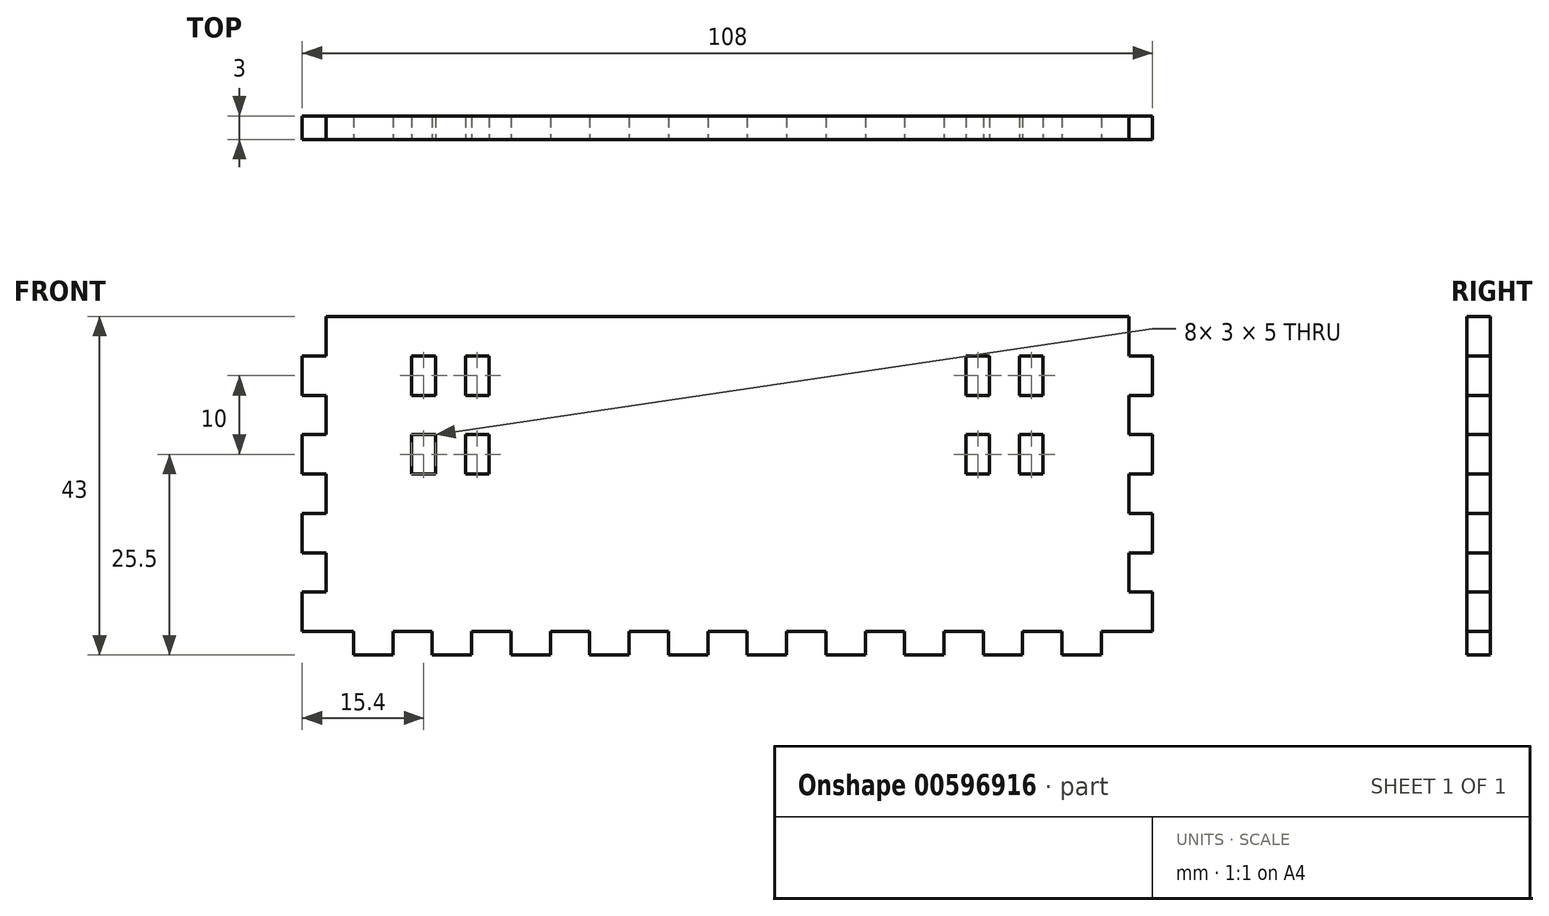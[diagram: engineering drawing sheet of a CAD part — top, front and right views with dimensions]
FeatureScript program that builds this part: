
annotation { "Feature Type Name" : "Feature", "Feature Type Description" : "" }
export const myFeature = defineFeature(function(context is Context, id is Id, definition is map)
    precondition{}
    {
        {
            var Q0;
            Q0=qCreatedBy(makeId("Front.planeOp"),FACE);
            var sketch = newSketch(context, id + "F0", { "sketchPlane" : qUnion([Q0])});
            skLineSegment(sketch, "E0.bottom", {"start": v(51, 20) * mm, "end": v(-51, 20) * mm});
            skLineSegment(sketch, "E0.top", {"start": v(51, -20) * mm, "end": v(-51, -20) * mm});
            skLineSegment(sketch, "E0.left", {"start": v(51, 20) * mm, "end": v(51, -20) * mm});
            skLineSegment(sketch, "E0.right", {"start": v(-51, 20) * mm, "end": v(-51, -20) * mm});
            skPoint(sketch, "E0.middle", {"position": v(0, 0) * mm});
            skSolve(sketch);
        }
        {
            var Q0;
            Q0=qSketchRegion(id+"F0",true);
            extrude(context, id + "F1", {"entities" : qUnion([Q0]), "depth" : 3 * mm, "offsetDistance" : 25 * mm});
        }
        {
            var Q0;
            Q0=makeQuery(id+"F1.opExtrude","CAP_FACE",FACE,{"disambiguationData":[OSD([sQuery(id+"F0.wireOp",EDGE,"E0.bottom"),sQuery(id+"F0.wireOp",EDGE,"E0.top"),sQuery(id+"F0.wireOp",EDGE,"E0.left"),sQuery(id+"F0.wireOp",EDGE,"E0.right")])],"isStart":false});
            var sketch = newSketch(context, id + "F2", { "sketchPlane" : qUnion([Q0])});
            skLineSegment(sketch, "E1.bottom", {"start": v(-51, -20) * mm, "end": v(-54, -20) * mm});
            skLineSegment(sketch, "E1.top", {"start": v(-51, -15) * mm, "end": v(-54, -15) * mm});
            skLineSegment(sketch, "E1.left", {"start": v(-51, -20) * mm, "end": v(-51, -15) * mm});
            skLineSegment(sketch, "E1.right", {"start": v(-54, -20) * mm, "end": v(-54, -15) * mm});
            skLineSegment(sketch, "E2.0.1.0", {"start": v(-51, -5) * mm, "end": v(-54, -5) * mm});
            skLineSegment(sketch, "E2.0.1.1", {"start": v(-54, -10) * mm, "end": v(-54, -5) * mm});
            skLineSegment(sketch, "E2.0.1.2", {"start": v(-51, -10) * mm, "end": v(-51, -5) * mm});
            skLineSegment(sketch, "E2.0.1.3", {"start": v(-51, -10) * mm, "end": v(-54, -10) * mm});
            skLineSegment(sketch, "E2.0.2.0", {"start": v(-51, 5) * mm, "end": v(-54, 5) * mm});
            skLineSegment(sketch, "E2.0.2.1", {"start": v(-54, 0) * mm, "end": v(-54, 5) * mm});
            skLineSegment(sketch, "E2.0.2.2", {"start": v(-51, 0) * mm, "end": v(-51, 5) * mm});
            skLineSegment(sketch, "E2.0.2.3", {"start": v(-51, 0) * mm, "end": v(-54, 0) * mm});
            skLineSegment(sketch, "E2.0.3.0", {"start": v(-51, 15) * mm, "end": v(-54, 15) * mm});
            skLineSegment(sketch, "E2.0.3.1", {"start": v(-54, 10) * mm, "end": v(-54, 15) * mm});
            skLineSegment(sketch, "E2.0.3.2", {"start": v(-51, 10) * mm, "end": v(-51, 15) * mm});
            skLineSegment(sketch, "E2.0.3.3", {"start": v(-51, 10) * mm, "end": v(-54, 10) * mm});
            skLineSegment(sketch, "E2.direction1", {"start": v(-54, -15) * mm, "end": v(-29, -15) * mm, "construction": true});
            skLineSegment(sketch, "E2.direction2", {"start": v(-54, -15) * mm, "end": v(-54, -5) * mm, "construction": true});
            skLineSegment(sketch, "E3.MirrorCS", {"start": v(54, -10) * mm, "end": v(54, -5) * mm});
            skLineSegment(sketch, "E4.MirrorCS", {"start": v(51, -5) * mm, "end": v(54, -5) * mm});
            skLineSegment(sketch, "E5.MirrorCS", {"start": v(51, -20) * mm, "end": v(51, -15) * mm});
            skLineSegment(sketch, "E6.MirrorCS", {"start": v(54, 10) * mm, "end": v(54, 15) * mm});
            skLineSegment(sketch, "E7.MirrorCS", {"start": v(51, -20) * mm, "end": v(54, -20) * mm});
            skLineSegment(sketch, "E8.MirrorCS", {"start": v(51, -15) * mm, "end": v(54, -15) * mm});
            skLineSegment(sketch, "E9.MirrorCS", {"start": v(54, -20) * mm, "end": v(54, -15) * mm});
            skLineSegment(sketch, "E10.MirrorCS", {"start": v(51, 15) * mm, "end": v(54, 15) * mm});
            skLineSegment(sketch, "E11.MirrorCS", {"start": v(51, 10) * mm, "end": v(54, 10) * mm});
            skLineSegment(sketch, "E12.MirrorCS", {"start": v(54, -15) * mm, "end": v(54, -5) * mm, "construction": true});
            skLineSegment(sketch, "E13.MirrorCS", {"start": v(51, 10) * mm, "end": v(51, 15) * mm});
            skLineSegment(sketch, "E14.MirrorCS", {"start": v(54, 0) * mm, "end": v(54, 5) * mm});
            skLineSegment(sketch, "E15.MirrorCS", {"start": v(51, 0) * mm, "end": v(51, 5) * mm});
            skLineSegment(sketch, "E16.MirrorCS", {"start": v(51, 0) * mm, "end": v(54, 0) * mm});
            skLineSegment(sketch, "E17.MirrorCS", {"start": v(51, -10) * mm, "end": v(51, -5) * mm});
            skLineSegment(sketch, "E18.MirrorCS", {"start": v(51, -10) * mm, "end": v(54, -10) * mm});
            skLineSegment(sketch, "E19.MirrorCS", {"start": v(51, 5) * mm, "end": v(54, 5) * mm});
            skSolve(sketch);
        }
        {
            var Q0;
            Q0=qSketchRegion(id+"F2",true);
            extrude(context, id + "F3", {"entities" : qUnion([Q0]), "operationType" : NewBodyOperationType.ADD, "oppositeDirection" : true, "depth" : 3 * mm, "offsetDistance" : 25 * mm});
        }
        {
            var Q0;
            Q0=makeQuery(id+"F3.boolean.opBoolean","MERGE",FACE,{"derivedFrom":[makeQuery(id+"F1.opExtrude","CAP_FACE",FACE,{"disambiguationData":[OSD([sQuery(id+"F0.wireOp",EDGE,"E0.bottom"),sQuery(id+"F0.wireOp",EDGE,"E0.top"),sQuery(id+"F0.wireOp",EDGE,"E0.left"),sQuery(id+"F0.wireOp",EDGE,"E0.right")])],"isStart":false}),makeQuery(id+"F3.opExtrude","CAP_FACE",FACE,{"disambiguationData":[OSD([sQuery(id+"F2.wireOp",EDGE,"E1.bottom"),sQuery(id+"F2.wireOp",EDGE,"E1.top"),sQuery(id+"F2.wireOp",EDGE,"E1.left"),sQuery(id+"F2.wireOp",EDGE,"E1.right")])],"isStart":true}),makeQuery(id+"F3.opExtrude","CAP_FACE",FACE,{"disambiguationData":[OSD([sQuery(id+"F2.wireOp",EDGE,"E2.0.1.0"),sQuery(id+"F2.wireOp",EDGE,"E2.0.1.1"),sQuery(id+"F2.wireOp",EDGE,"E2.0.1.2"),sQuery(id+"F2.wireOp",EDGE,"E2.0.1.3")])],"isStart":true}),makeQuery(id+"F3.opExtrude","CAP_FACE",FACE,{"disambiguationData":[OSD([sQuery(id+"F2.wireOp",EDGE,"E2.0.2.0"),sQuery(id+"F2.wireOp",EDGE,"E2.0.2.1"),sQuery(id+"F2.wireOp",EDGE,"E2.0.2.2"),sQuery(id+"F2.wireOp",EDGE,"E2.0.2.3")])],"isStart":true}),makeQuery(id+"F3.opExtrude","CAP_FACE",FACE,{"disambiguationData":[OSD([sQuery(id+"F2.wireOp",EDGE,"E2.0.3.0"),sQuery(id+"F2.wireOp",EDGE,"E2.0.3.1"),sQuery(id+"F2.wireOp",EDGE,"E2.0.3.2"),sQuery(id+"F2.wireOp",EDGE,"E2.0.3.3")])],"isStart":true}),makeQuery(id+"F3.opExtrude","CAP_FACE",FACE,{"disambiguationData":[OSD([sQuery(id+"F2.wireOp",EDGE,"E3.MirrorCS"),sQuery(id+"F2.wireOp",EDGE,"E4.MirrorCS"),sQuery(id+"F2.wireOp",EDGE,"E17.MirrorCS"),sQuery(id+"F2.wireOp",EDGE,"E18.MirrorCS")])],"isStart":true}),makeQuery(id+"F3.opExtrude","CAP_FACE",FACE,{"disambiguationData":[OSD([sQuery(id+"F2.wireOp",EDGE,"E5.MirrorCS"),sQuery(id+"F2.wireOp",EDGE,"E7.MirrorCS"),sQuery(id+"F2.wireOp",EDGE,"E8.MirrorCS"),sQuery(id+"F2.wireOp",EDGE,"E9.MirrorCS")])],"isStart":true}),makeQuery(id+"F3.opExtrude","CAP_FACE",FACE,{"disambiguationData":[OSD([sQuery(id+"F2.wireOp",EDGE,"E6.MirrorCS"),sQuery(id+"F2.wireOp",EDGE,"E10.MirrorCS"),sQuery(id+"F2.wireOp",EDGE,"E11.MirrorCS"),sQuery(id+"F2.wireOp",EDGE,"E13.MirrorCS")])],"isStart":true}),makeQuery(id+"F3.opExtrude","CAP_FACE",FACE,{"disambiguationData":[OSD([sQuery(id+"F2.wireOp",EDGE,"E14.MirrorCS"),sQuery(id+"F2.wireOp",EDGE,"E15.MirrorCS"),sQuery(id+"F2.wireOp",EDGE,"E16.MirrorCS"),sQuery(id+"F2.wireOp",EDGE,"E19.MirrorCS")])],"isStart":true})]});
            var sketch = newSketch(context, id + "F4", { "sketchPlane" : qUnion([Q0])});
            skLineSegment(sketch, "E20", {"start": v(0, -20) * mm, "end": v(0, -23) * mm, "construction": true});
            skPoint(sketch, "E20.endSnap0", {"position": v(0, -20) * mm});
            skLineSegment(sketch, "E21", {"start": v(0, -23) * mm, "end": v(2.5, -23) * mm, "construction": true});
            skLineSegment(sketch, "E22.bottom", {"start": v(2.5, -23) * mm, "end": v(7.5, -23) * mm});
            skLineSegment(sketch, "E22.top", {"start": v(2.5, -20) * mm, "end": v(7.5, -20) * mm});
            skLineSegment(sketch, "E22.left", {"start": v(2.5, -23) * mm, "end": v(2.5, -20) * mm});
            skLineSegment(sketch, "E22.right", {"start": v(7.5, -23) * mm, "end": v(7.5, -20) * mm});
            skLineSegment(sketch, "E23.1.0.0", {"start": v(12.5, -23) * mm, "end": v(17.5, -23) * mm});
            skLineSegment(sketch, "E23.1.0.1", {"start": v(12.5, -23) * mm, "end": v(12.5, -20) * mm});
            skLineSegment(sketch, "E23.1.0.2", {"start": v(17.5, -23) * mm, "end": v(17.5, -20) * mm});
            skLineSegment(sketch, "E23.1.0.3", {"start": v(12.5, -20) * mm, "end": v(17.5, -20) * mm});
            skLineSegment(sketch, "E23.2.0.0", {"start": v(22.5, -23) * mm, "end": v(27.5, -23) * mm});
            skLineSegment(sketch, "E23.2.0.1", {"start": v(22.5, -23) * mm, "end": v(22.5, -20) * mm});
            skLineSegment(sketch, "E23.2.0.2", {"start": v(27.5, -23) * mm, "end": v(27.5, -20) * mm});
            skLineSegment(sketch, "E23.2.0.3", {"start": v(22.5, -20) * mm, "end": v(27.5, -20) * mm});
            skLineSegment(sketch, "E23.3.0.0", {"start": v(32.5, -23) * mm, "end": v(37.5, -23) * mm});
            skLineSegment(sketch, "E23.3.0.1", {"start": v(32.5, -23) * mm, "end": v(32.5, -20) * mm});
            skLineSegment(sketch, "E23.3.0.2", {"start": v(37.5, -23) * mm, "end": v(37.5, -20) * mm});
            skLineSegment(sketch, "E23.3.0.3", {"start": v(32.5, -20) * mm, "end": v(37.5, -20) * mm});
            skLineSegment(sketch, "E23.4.0.0", {"start": v(42.5, -23) * mm, "end": v(47.5, -23) * mm});
            skLineSegment(sketch, "E23.4.0.1", {"start": v(42.5, -23) * mm, "end": v(42.5, -20) * mm});
            skLineSegment(sketch, "E23.4.0.2", {"start": v(47.5, -23) * mm, "end": v(47.5, -20) * mm});
            skLineSegment(sketch, "E23.4.0.3", {"start": v(42.5, -20) * mm, "end": v(47.5, -20) * mm});
            skLineSegment(sketch, "E23.direction1", {"start": v(2.5, -23) * mm, "end": v(12.5, -23) * mm, "construction": true});
            skLineSegment(sketch, "E24.MirrorCS", {"start": v(-27.5, -23) * mm, "end": v(-27.5, -20) * mm});
            skLineSegment(sketch, "E25.MirrorCS", {"start": v(-22.5, -23) * mm, "end": v(-22.5, -20) * mm});
            skLineSegment(sketch, "E26.MirrorCS", {"start": v(-17.5, -23) * mm, "end": v(-17.5, -20) * mm});
            skLineSegment(sketch, "E27.MirrorCS", {"start": v(-12.5, -23) * mm, "end": v(-12.5, -20) * mm});
            skLineSegment(sketch, "E28.MirrorCS", {"start": v(-7.5, -23) * mm, "end": v(-7.5, -20) * mm});
            skLineSegment(sketch, "E29.MirrorCS", {"start": v(-2.5, -23) * mm, "end": v(-2.5, -20) * mm});
            skLineSegment(sketch, "E30.MirrorCS", {"start": v(-32.5, -23) * mm, "end": v(-32.5, -20) * mm});
            skLineSegment(sketch, "E31.MirrorCS", {"start": v(-47.5, -23) * mm, "end": v(-47.5, -20) * mm});
            skLineSegment(sketch, "E32.MirrorCS", {"start": v(-37.5, -23) * mm, "end": v(-37.5, -20) * mm});
            skLineSegment(sketch, "E33.MirrorCS", {"start": v(-42.5, -23) * mm, "end": v(-42.5, -20) * mm});
            skLineSegment(sketch, "E34.MirrorCS", {"start": v(-2.5, -23) * mm, "end": v(-7.5, -23) * mm});
            skLineSegment(sketch, "E35.MirrorCS", {"start": v(-32.5, -20) * mm, "end": v(-37.5, -20) * mm});
            skLineSegment(sketch, "E36.MirrorCS", {"start": v(-42.5, -20) * mm, "end": v(-47.5, -20) * mm});
            skLineSegment(sketch, "E37.MirrorCS", {"start": v(-22.5, -23) * mm, "end": v(-27.5, -23) * mm});
            skLineSegment(sketch, "E38.MirrorCS", {"start": v(-12.5, -20) * mm, "end": v(-17.5, -20) * mm});
            skLineSegment(sketch, "E39.MirrorCS", {"start": v(-12.5, -23) * mm, "end": v(-17.5, -23) * mm});
            skLineSegment(sketch, "E40.MirrorCS", {"start": v(-2.5, -20) * mm, "end": v(-7.5, -20) * mm});
            skLineSegment(sketch, "E41.MirrorCS", {"start": v(-32.5, -23) * mm, "end": v(-37.5, -23) * mm});
            skLineSegment(sketch, "E42.MirrorCS", {"start": v(-22.5, -20) * mm, "end": v(-27.5, -20) * mm});
            skLineSegment(sketch, "E43.MirrorCS", {"start": v(-42.5, -23) * mm, "end": v(-47.5, -23) * mm});
            skLineSegment(sketch, "E44.MirrorCS", {"start": v(-2.5, -23) * mm, "end": v(-12.5, -23) * mm, "construction": true});
            skSolve(sketch);
        }
        {
            var Q0;
            Q0=qSketchRegion(id+"F4",true);
            extrude(context, id + "F5", {"entities" : qUnion([Q0]), "operationType" : NewBodyOperationType.ADD, "oppositeDirection" : true, "depth" : 3 * mm, "offsetDistance" : 25 * mm});
        }
        {
            var Q0;
            Q0=makeQuery(id+"F5.boolean.opBoolean","MERGE",FACE,{"derivedFrom":[makeQuery(id+"F3.boolean.opBoolean","MERGE",FACE,{"derivedFrom":[makeQuery(id+"F1.opExtrude","CAP_FACE",FACE,{"disambiguationData":[OSD([sQuery(id+"F0.wireOp",EDGE,"E0.bottom"),sQuery(id+"F0.wireOp",EDGE,"E0.top"),sQuery(id+"F0.wireOp",EDGE,"E0.left"),sQuery(id+"F0.wireOp",EDGE,"E0.right")])],"isStart":false}),makeQuery(id+"F3.opExtrude","CAP_FACE",FACE,{"disambiguationData":[OSD([sQuery(id+"F2.wireOp",EDGE,"E1.bottom"),sQuery(id+"F2.wireOp",EDGE,"E1.top"),sQuery(id+"F2.wireOp",EDGE,"E1.left"),sQuery(id+"F2.wireOp",EDGE,"E1.right")])],"isStart":true}),makeQuery(id+"F3.opExtrude","CAP_FACE",FACE,{"disambiguationData":[OSD([sQuery(id+"F2.wireOp",EDGE,"E2.0.1.0"),sQuery(id+"F2.wireOp",EDGE,"E2.0.1.1"),sQuery(id+"F2.wireOp",EDGE,"E2.0.1.2"),sQuery(id+"F2.wireOp",EDGE,"E2.0.1.3")])],"isStart":true}),makeQuery(id+"F3.opExtrude","CAP_FACE",FACE,{"disambiguationData":[OSD([sQuery(id+"F2.wireOp",EDGE,"E2.0.2.0"),sQuery(id+"F2.wireOp",EDGE,"E2.0.2.1"),sQuery(id+"F2.wireOp",EDGE,"E2.0.2.2"),sQuery(id+"F2.wireOp",EDGE,"E2.0.2.3")])],"isStart":true}),makeQuery(id+"F3.opExtrude","CAP_FACE",FACE,{"disambiguationData":[OSD([sQuery(id+"F2.wireOp",EDGE,"E2.0.3.0"),sQuery(id+"F2.wireOp",EDGE,"E2.0.3.1"),sQuery(id+"F2.wireOp",EDGE,"E2.0.3.2"),sQuery(id+"F2.wireOp",EDGE,"E2.0.3.3")])],"isStart":true}),makeQuery(id+"F3.opExtrude","CAP_FACE",FACE,{"disambiguationData":[OSD([sQuery(id+"F2.wireOp",EDGE,"E3.MirrorCS"),sQuery(id+"F2.wireOp",EDGE,"E4.MirrorCS"),sQuery(id+"F2.wireOp",EDGE,"E17.MirrorCS"),sQuery(id+"F2.wireOp",EDGE,"E18.MirrorCS")])],"isStart":true}),makeQuery(id+"F3.opExtrude","CAP_FACE",FACE,{"disambiguationData":[OSD([sQuery(id+"F2.wireOp",EDGE,"E5.MirrorCS"),sQuery(id+"F2.wireOp",EDGE,"E7.MirrorCS"),sQuery(id+"F2.wireOp",EDGE,"E8.MirrorCS"),sQuery(id+"F2.wireOp",EDGE,"E9.MirrorCS")])],"isStart":true}),makeQuery(id+"F3.opExtrude","CAP_FACE",FACE,{"disambiguationData":[OSD([sQuery(id+"F2.wireOp",EDGE,"E6.MirrorCS"),sQuery(id+"F2.wireOp",EDGE,"E10.MirrorCS"),sQuery(id+"F2.wireOp",EDGE,"E11.MirrorCS"),sQuery(id+"F2.wireOp",EDGE,"E13.MirrorCS")])],"isStart":true}),makeQuery(id+"F3.opExtrude","CAP_FACE",FACE,{"disambiguationData":[OSD([sQuery(id+"F2.wireOp",EDGE,"E14.MirrorCS"),sQuery(id+"F2.wireOp",EDGE,"E15.MirrorCS"),sQuery(id+"F2.wireOp",EDGE,"E16.MirrorCS"),sQuery(id+"F2.wireOp",EDGE,"E19.MirrorCS")])],"isStart":true})]}),makeQuery(id+"F5.opExtrude","CAP_FACE",FACE,{"disambiguationData":[OSD([sQuery(id+"F4.wireOp",EDGE,"E22.bottom"),sQuery(id+"F4.wireOp",EDGE,"E22.top"),sQuery(id+"F4.wireOp",EDGE,"E22.left"),sQuery(id+"F4.wireOp",EDGE,"E22.right")])],"isStart":true}),makeQuery(id+"F5.opExtrude","CAP_FACE",FACE,{"disambiguationData":[OSD([sQuery(id+"F4.wireOp",EDGE,"E23.1.0.0"),sQuery(id+"F4.wireOp",EDGE,"E23.1.0.1"),sQuery(id+"F4.wireOp",EDGE,"E23.1.0.2"),sQuery(id+"F4.wireOp",EDGE,"E23.1.0.3")])],"isStart":true}),makeQuery(id+"F5.opExtrude","CAP_FACE",FACE,{"disambiguationData":[OSD([sQuery(id+"F4.wireOp",EDGE,"E23.2.0.0"),sQuery(id+"F4.wireOp",EDGE,"E23.2.0.1"),sQuery(id+"F4.wireOp",EDGE,"E23.2.0.2"),sQuery(id+"F4.wireOp",EDGE,"E23.2.0.3")])],"isStart":true}),makeQuery(id+"F5.opExtrude","CAP_FACE",FACE,{"disambiguationData":[OSD([sQuery(id+"F4.wireOp",EDGE,"E23.3.0.0"),sQuery(id+"F4.wireOp",EDGE,"E23.3.0.1"),sQuery(id+"F4.wireOp",EDGE,"E23.3.0.2"),sQuery(id+"F4.wireOp",EDGE,"E23.3.0.3")])],"isStart":true}),makeQuery(id+"F5.opExtrude","CAP_FACE",FACE,{"disambiguationData":[OSD([sQuery(id+"F4.wireOp",EDGE,"E23.4.0.0"),sQuery(id+"F4.wireOp",EDGE,"E23.4.0.1"),sQuery(id+"F4.wireOp",EDGE,"E23.4.0.2"),sQuery(id+"F4.wireOp",EDGE,"E23.4.0.3")])],"isStart":true}),makeQuery(id+"F5.opExtrude","CAP_FACE",FACE,{"disambiguationData":[OSD([sQuery(id+"F4.wireOp",EDGE,"E24.MirrorCS"),sQuery(id+"F4.wireOp",EDGE,"E25.MirrorCS"),sQuery(id+"F4.wireOp",EDGE,"E37.MirrorCS"),sQuery(id+"F4.wireOp",EDGE,"E42.MirrorCS")])],"isStart":true}),makeQuery(id+"F5.opExtrude","CAP_FACE",FACE,{"disambiguationData":[OSD([sQuery(id+"F4.wireOp",EDGE,"E26.MirrorCS"),sQuery(id+"F4.wireOp",EDGE,"E27.MirrorCS"),sQuery(id+"F4.wireOp",EDGE,"E38.MirrorCS"),sQuery(id+"F4.wireOp",EDGE,"E39.MirrorCS")])],"isStart":true}),makeQuery(id+"F5.opExtrude","CAP_FACE",FACE,{"disambiguationData":[OSD([sQuery(id+"F4.wireOp",EDGE,"E28.MirrorCS"),sQuery(id+"F4.wireOp",EDGE,"E29.MirrorCS"),sQuery(id+"F4.wireOp",EDGE,"E34.MirrorCS"),sQuery(id+"F4.wireOp",EDGE,"E40.MirrorCS")])],"isStart":true}),makeQuery(id+"F5.opExtrude","CAP_FACE",FACE,{"disambiguationData":[OSD([sQuery(id+"F4.wireOp",EDGE,"E30.MirrorCS"),sQuery(id+"F4.wireOp",EDGE,"E32.MirrorCS"),sQuery(id+"F4.wireOp",EDGE,"E35.MirrorCS"),sQuery(id+"F4.wireOp",EDGE,"E41.MirrorCS")])],"isStart":true}),makeQuery(id+"F5.opExtrude","CAP_FACE",FACE,{"disambiguationData":[OSD([sQuery(id+"F4.wireOp",EDGE,"E31.MirrorCS"),sQuery(id+"F4.wireOp",EDGE,"E33.MirrorCS"),sQuery(id+"F4.wireOp",EDGE,"E36.MirrorCS"),sQuery(id+"F4.wireOp",EDGE,"E43.MirrorCS")])],"isStart":true})]});
            var sketch = newSketch(context, id + "F6", { "sketchPlane" : qUnion([Q0])});
            skLineSegment(sketch, "E45", {"start": v(0, 20) * mm, "end": v(-32, 20) * mm, "construction": true});
            skLineSegment(sketch, "E46", {"start": v(-32, 20) * mm, "end": v(-32, 12.5) * mm, "construction": true});
            skLineSegment(sketch, "E47.bottom", {"start": v(-33.5, 10) * mm, "end": v(-30.5, 10) * mm});
            skLineSegment(sketch, "E47.top", {"start": v(-33.5, 15) * mm, "end": v(-30.5, 15) * mm});
            skLineSegment(sketch, "E47.left", {"start": v(-33.5, 10) * mm, "end": v(-33.5, 15) * mm});
            skLineSegment(sketch, "E47.right", {"start": v(-30.5, 10) * mm, "end": v(-30.5, 15) * mm});
            skPoint(sketch, "E47.middle", {"position": v(-32, 12.5) * mm});
            skLineSegment(sketch, "E48.0.1.0", {"start": v(-33.5, 0) * mm, "end": v(-30.5, 0) * mm});
            skLineSegment(sketch, "E48.0.1.1", {"start": v(-33.5, 0) * mm, "end": v(-33.5, 5) * mm});
            skLineSegment(sketch, "E48.0.1.2", {"start": v(-30.5, 0) * mm, "end": v(-30.5, 5) * mm});
            skLineSegment(sketch, "E48.0.1.3", {"start": v(-33.5, 5) * mm, "end": v(-30.5, 5) * mm});
            skLineSegment(sketch, "E48.direction1", {"start": v(-33.5, 10) * mm, "end": v(-8.5, 10) * mm, "construction": true});
            skLineSegment(sketch, "E48.direction2", {"start": v(-33.5, 10) * mm, "end": v(-33.5, 0) * mm, "construction": true});
            skLineSegment(sketch, "E49.MirrorCS", {"start": v(33.5, 0) * mm, "end": v(30.5, 0) * mm});
            skLineSegment(sketch, "E50.MirrorCS", {"start": v(33.5, 15) * mm, "end": v(30.5, 15) * mm});
            skLineSegment(sketch, "E51.MirrorCS", {"start": v(33.5, 10) * mm, "end": v(30.5, 10) * mm});
            skLineSegment(sketch, "E52.MirrorCS", {"start": v(33.5, 5) * mm, "end": v(30.5, 5) * mm});
            skLineSegment(sketch, "E53.MirrorCS", {"start": v(33.5, 0) * mm, "end": v(33.5, 5) * mm});
            skLineSegment(sketch, "E54.MirrorCS", {"start": v(30.5, 10) * mm, "end": v(30.5, 15) * mm});
            skLineSegment(sketch, "E55.MirrorCS", {"start": v(33.5, 10) * mm, "end": v(33.5, 15) * mm});
            skLineSegment(sketch, "E56.MirrorCS", {"start": v(32, 20) * mm, "end": v(32, 12.5) * mm, "construction": true});
            skLineSegment(sketch, "E57.MirrorCS", {"start": v(30.5, 0) * mm, "end": v(30.5, 5) * mm});
            skLineSegment(sketch, "E58.MirrorCS", {"start": v(33.5, 10) * mm, "end": v(33.5, 0) * mm, "construction": true});
            skPoint(sketch, "E59.MirrorP", {"position": v(32, 12.5) * mm});
            skLineSegment(sketch, "E60", {"start": v(-32, 20) * mm, "end": v(-35.2, 20) * mm, "construction": true});
            skLineSegment(sketch, "E61", {"start": v(-35.2, 20) * mm, "end": v(-35.2, 16.67) * mm, "construction": true});
            skLineSegment(sketch, "E62.MirrorCS", {"start": v(-36.9, 0) * mm, "end": v(-36.9, 5) * mm});
            skLineSegment(sketch, "E63.MirrorCS", {"start": v(-36.9, 0) * mm, "end": v(-39.9, 0) * mm});
            skLineSegment(sketch, "E64.MirrorCS", {"start": v(-39.9, 0) * mm, "end": v(-39.9, 5) * mm});
            skLineSegment(sketch, "E65.MirrorCS", {"start": v(-36.9, 5) * mm, "end": v(-39.9, 5) * mm});
            skLineSegment(sketch, "E66.MirrorCS", {"start": v(-36.9, 10) * mm, "end": v(-36.9, 0) * mm, "construction": true});
            skPoint(sketch, "E67.MirrorP", {"position": v(-38.4, 12.5) * mm});
            skLineSegment(sketch, "E68.MirrorCS", {"start": v(-39.9, 10) * mm, "end": v(-39.9, 15) * mm});
            skLineSegment(sketch, "E69.MirrorCS", {"start": v(-36.9, 10) * mm, "end": v(-36.9, 15) * mm});
            skLineSegment(sketch, "E70.MirrorCS", {"start": v(-36.9, 15) * mm, "end": v(-39.9, 15) * mm});
            skLineSegment(sketch, "E71.MirrorCS", {"start": v(-36.9, 10) * mm, "end": v(-39.9, 10) * mm});
            skLineSegment(sketch, "E72.MirrorCS", {"start": v(36.9, 10) * mm, "end": v(39.9, 10) * mm});
            skPoint(sketch, "E73.MirrorP", {"position": v(38.4, 12.5) * mm});
            skLineSegment(sketch, "E74.MirrorCS", {"start": v(39.9, 0) * mm, "end": v(39.9, 5) * mm});
            skLineSegment(sketch, "E75.MirrorCS", {"start": v(36.9, 15) * mm, "end": v(39.9, 15) * mm});
            skLineSegment(sketch, "E76.MirrorCS", {"start": v(36.9, 0) * mm, "end": v(39.9, 0) * mm});
            skLineSegment(sketch, "E77.MirrorCS", {"start": v(36.9, 0) * mm, "end": v(36.9, 5) * mm});
            skLineSegment(sketch, "E78.MirrorCS", {"start": v(36.9, 10) * mm, "end": v(36.9, 15) * mm});
            skLineSegment(sketch, "E79.MirrorCS", {"start": v(36.9, 5) * mm, "end": v(39.9, 5) * mm});
            skLineSegment(sketch, "E80.MirrorCS", {"start": v(36.9, 10) * mm, "end": v(36.9, 0) * mm, "construction": true});
            skLineSegment(sketch, "E81.MirrorCS", {"start": v(39.9, 10) * mm, "end": v(39.9, 15) * mm});
            skSolve(sketch);
        }
        {
            var Q0;
            Q0 = qSketchRegion(id + "F6", true);
            extrude(context, id + "F7", {"entities" : qUnion([Q0]), "operationType" : NewBodyOperationType.REMOVE, "oppositeDirection" : true, "depth" : 25 * mm, "offsetDistance" : 25 * mm});
        }
        {
            var Q0;
            Q0=makeQuery(id+"F5.boolean.opBoolean","MERGE",FACE,{"derivedFrom":[makeQuery(id+"F3.boolean.opBoolean","MERGE",FACE,{"derivedFrom":[makeQuery(id+"F1.opExtrude","CAP_FACE",FACE,{"disambiguationData":[OSD([sQuery(id+"F0.wireOp",EDGE,"E0.bottom"),sQuery(id+"F0.wireOp",EDGE,"E0.top"),sQuery(id+"F0.wireOp",EDGE,"E0.left"),sQuery(id+"F0.wireOp",EDGE,"E0.right")])],"isStart":false}),makeQuery(id+"F3.opExtrude","CAP_FACE",FACE,{"disambiguationData":[OSD([sQuery(id+"F2.wireOp",EDGE,"E1.bottom"),sQuery(id+"F2.wireOp",EDGE,"E1.top"),sQuery(id+"F2.wireOp",EDGE,"E1.left"),sQuery(id+"F2.wireOp",EDGE,"E1.right")])],"isStart":true}),makeQuery(id+"F3.opExtrude","CAP_FACE",FACE,{"disambiguationData":[OSD([sQuery(id+"F2.wireOp",EDGE,"E2.0.1.0"),sQuery(id+"F2.wireOp",EDGE,"E2.0.1.1"),sQuery(id+"F2.wireOp",EDGE,"E2.0.1.2"),sQuery(id+"F2.wireOp",EDGE,"E2.0.1.3")])],"isStart":true}),makeQuery(id+"F3.opExtrude","CAP_FACE",FACE,{"disambiguationData":[OSD([sQuery(id+"F2.wireOp",EDGE,"E2.0.2.0"),sQuery(id+"F2.wireOp",EDGE,"E2.0.2.1"),sQuery(id+"F2.wireOp",EDGE,"E2.0.2.2"),sQuery(id+"F2.wireOp",EDGE,"E2.0.2.3")])],"isStart":true}),makeQuery(id+"F3.opExtrude","CAP_FACE",FACE,{"disambiguationData":[OSD([sQuery(id+"F2.wireOp",EDGE,"E2.0.3.0"),sQuery(id+"F2.wireOp",EDGE,"E2.0.3.1"),sQuery(id+"F2.wireOp",EDGE,"E2.0.3.2"),sQuery(id+"F2.wireOp",EDGE,"E2.0.3.3")])],"isStart":true}),makeQuery(id+"F3.opExtrude","CAP_FACE",FACE,{"disambiguationData":[OSD([sQuery(id+"F2.wireOp",EDGE,"E3.MirrorCS"),sQuery(id+"F2.wireOp",EDGE,"E4.MirrorCS"),sQuery(id+"F2.wireOp",EDGE,"E17.MirrorCS"),sQuery(id+"F2.wireOp",EDGE,"E18.MirrorCS")])],"isStart":true}),makeQuery(id+"F3.opExtrude","CAP_FACE",FACE,{"disambiguationData":[OSD([sQuery(id+"F2.wireOp",EDGE,"E5.MirrorCS"),sQuery(id+"F2.wireOp",EDGE,"E7.MirrorCS"),sQuery(id+"F2.wireOp",EDGE,"E8.MirrorCS"),sQuery(id+"F2.wireOp",EDGE,"E9.MirrorCS")])],"isStart":true}),makeQuery(id+"F3.opExtrude","CAP_FACE",FACE,{"disambiguationData":[OSD([sQuery(id+"F2.wireOp",EDGE,"E6.MirrorCS"),sQuery(id+"F2.wireOp",EDGE,"E10.MirrorCS"),sQuery(id+"F2.wireOp",EDGE,"E11.MirrorCS"),sQuery(id+"F2.wireOp",EDGE,"E13.MirrorCS")])],"isStart":true}),makeQuery(id+"F3.opExtrude","CAP_FACE",FACE,{"disambiguationData":[OSD([sQuery(id+"F2.wireOp",EDGE,"E14.MirrorCS"),sQuery(id+"F2.wireOp",EDGE,"E15.MirrorCS"),sQuery(id+"F2.wireOp",EDGE,"E16.MirrorCS"),sQuery(id+"F2.wireOp",EDGE,"E19.MirrorCS")])],"isStart":true})]}),makeQuery(id+"F5.opExtrude","CAP_FACE",FACE,{"disambiguationData":[OSD([sQuery(id+"F4.wireOp",EDGE,"E22.bottom"),sQuery(id+"F4.wireOp",EDGE,"E22.top"),sQuery(id+"F4.wireOp",EDGE,"E22.left"),sQuery(id+"F4.wireOp",EDGE,"E22.right")])],"isStart":true}),makeQuery(id+"F5.opExtrude","CAP_FACE",FACE,{"disambiguationData":[OSD([sQuery(id+"F4.wireOp",EDGE,"E23.1.0.0"),sQuery(id+"F4.wireOp",EDGE,"E23.1.0.1"),sQuery(id+"F4.wireOp",EDGE,"E23.1.0.2"),sQuery(id+"F4.wireOp",EDGE,"E23.1.0.3")])],"isStart":true}),makeQuery(id+"F5.opExtrude","CAP_FACE",FACE,{"disambiguationData":[OSD([sQuery(id+"F4.wireOp",EDGE,"E23.2.0.0"),sQuery(id+"F4.wireOp",EDGE,"E23.2.0.1"),sQuery(id+"F4.wireOp",EDGE,"E23.2.0.2"),sQuery(id+"F4.wireOp",EDGE,"E23.2.0.3")])],"isStart":true}),makeQuery(id+"F5.opExtrude","CAP_FACE",FACE,{"disambiguationData":[OSD([sQuery(id+"F4.wireOp",EDGE,"E23.3.0.0"),sQuery(id+"F4.wireOp",EDGE,"E23.3.0.1"),sQuery(id+"F4.wireOp",EDGE,"E23.3.0.2"),sQuery(id+"F4.wireOp",EDGE,"E23.3.0.3")])],"isStart":true}),makeQuery(id+"F5.opExtrude","CAP_FACE",FACE,{"disambiguationData":[OSD([sQuery(id+"F4.wireOp",EDGE,"E23.4.0.0"),sQuery(id+"F4.wireOp",EDGE,"E23.4.0.1"),sQuery(id+"F4.wireOp",EDGE,"E23.4.0.2"),sQuery(id+"F4.wireOp",EDGE,"E23.4.0.3")])],"isStart":true}),makeQuery(id+"F5.opExtrude","CAP_FACE",FACE,{"disambiguationData":[OSD([sQuery(id+"F4.wireOp",EDGE,"E24.MirrorCS"),sQuery(id+"F4.wireOp",EDGE,"E25.MirrorCS"),sQuery(id+"F4.wireOp",EDGE,"E37.MirrorCS"),sQuery(id+"F4.wireOp",EDGE,"E42.MirrorCS")])],"isStart":true}),makeQuery(id+"F5.opExtrude","CAP_FACE",FACE,{"disambiguationData":[OSD([sQuery(id+"F4.wireOp",EDGE,"E26.MirrorCS"),sQuery(id+"F4.wireOp",EDGE,"E27.MirrorCS"),sQuery(id+"F4.wireOp",EDGE,"E38.MirrorCS"),sQuery(id+"F4.wireOp",EDGE,"E39.MirrorCS")])],"isStart":true}),makeQuery(id+"F5.opExtrude","CAP_FACE",FACE,{"disambiguationData":[OSD([sQuery(id+"F4.wireOp",EDGE,"E28.MirrorCS"),sQuery(id+"F4.wireOp",EDGE,"E29.MirrorCS"),sQuery(id+"F4.wireOp",EDGE,"E34.MirrorCS"),sQuery(id+"F4.wireOp",EDGE,"E40.MirrorCS")])],"isStart":true}),makeQuery(id+"F5.opExtrude","CAP_FACE",FACE,{"disambiguationData":[OSD([sQuery(id+"F4.wireOp",EDGE,"E30.MirrorCS"),sQuery(id+"F4.wireOp",EDGE,"E32.MirrorCS"),sQuery(id+"F4.wireOp",EDGE,"E35.MirrorCS"),sQuery(id+"F4.wireOp",EDGE,"E41.MirrorCS")])],"isStart":true}),makeQuery(id+"F5.opExtrude","CAP_FACE",FACE,{"disambiguationData":[OSD([sQuery(id+"F4.wireOp",EDGE,"E31.MirrorCS"),sQuery(id+"F4.wireOp",EDGE,"E33.MirrorCS"),sQuery(id+"F4.wireOp",EDGE,"E36.MirrorCS"),sQuery(id+"F4.wireOp",EDGE,"E43.MirrorCS")])],"isStart":true})]});
            var sketch = newSketch(context, id + "F8", { "sketchPlane" : qUnion([Q0])});
            skLineSegment(sketch, "E82.bottom", {"start": v(-33.5, 15) * mm, "end": v(-33.3, 15) * mm});
            skLineSegment(sketch, "E82.top", {"start": v(-33.5, 10) * mm, "end": v(-33.3, 10) * mm});
            skLineSegment(sketch, "E82.left", {"start": v(-33.5, 15) * mm, "end": v(-33.5, 10) * mm});
            skLineSegment(sketch, "E82.right", {"start": v(-33.3, 15) * mm, "end": v(-33.3, 10) * mm});
            skLineSegment(sketch, "E83.bottom", {"start": v(-36.9, 15) * mm, "end": v(-37.1, 15) * mm});
            skLineSegment(sketch, "E83.top", {"start": v(-36.9, 10) * mm, "end": v(-37.1, 10) * mm});
            skLineSegment(sketch, "E83.left", {"start": v(-36.9, 15) * mm, "end": v(-36.9, 10) * mm});
            skLineSegment(sketch, "E83.right", {"start": v(-37.1, 15) * mm, "end": v(-37.1, 10) * mm});
            skLineSegment(sketch, "E84", {"start": v(-36.9, 5) * mm, "end": v(-33.5, 5) * mm, "construction": true});
            skLineSegment(sketch, "E85", {"start": v(-33.5, 5) * mm, "end": v(-35.2, 5) * mm, "construction": true});
            skLineSegment(sketch, "E86", {"start": v(-35.2, 5) * mm, "end": v(-35.2, 10) * mm, "construction": true});
            skLineSegment(sketch, "E87", {"start": v(-35.2, 10) * mm, "end": v(-35.2, 7.5) * mm, "construction": true});
            skLineSegment(sketch, "E88", {"start": v(-35.2, 7.5) * mm, "end": v(-33.5, 7.5) * mm, "construction": true});
            skLineSegment(sketch, "E89.MirrorCS", {"start": v(-36.9, 5) * mm, "end": v(-37.1, 5) * mm});
            skLineSegment(sketch, "E90.MirrorCS", {"start": v(-36.9, 0) * mm, "end": v(-37.1, 0) * mm});
            skLineSegment(sketch, "E91.MirrorCS", {"start": v(-33.5, 5) * mm, "end": v(-33.3, 5) * mm});
            skLineSegment(sketch, "E92.MirrorCS", {"start": v(-33.5, 0) * mm, "end": v(-33.3, 0) * mm});
            skLineSegment(sketch, "E93.MirrorCS", {"start": v(-36.9, 0) * mm, "end": v(-36.9, 5) * mm});
            skLineSegment(sketch, "E94.MirrorCS", {"start": v(-33.5, 0) * mm, "end": v(-33.5, 5) * mm});
            skLineSegment(sketch, "E95.MirrorCS", {"start": v(-37.1, 0) * mm, "end": v(-37.1, 5) * mm});
            skLineSegment(sketch, "E96.MirrorCS", {"start": v(-33.3, 0) * mm, "end": v(-33.3, 5) * mm});
            skLineSegment(sketch, "E97.MirrorCS", {"start": v(33.5, 5) * mm, "end": v(33.3, 5) * mm});
            skLineSegment(sketch, "E98.MirrorCS", {"start": v(33.5, 0) * mm, "end": v(33.3, 0) * mm});
            skLineSegment(sketch, "E99.MirrorCS", {"start": v(36.9, 5) * mm, "end": v(37.1, 5) * mm});
            skLineSegment(sketch, "E100.MirrorCS", {"start": v(36.9, 0) * mm, "end": v(37.1, 0) * mm});
            skLineSegment(sketch, "E101.MirrorCS", {"start": v(33.5, 10) * mm, "end": v(33.3, 10) * mm});
            skLineSegment(sketch, "E102.MirrorCS", {"start": v(33.5, 15) * mm, "end": v(33.3, 15) * mm});
            skLineSegment(sketch, "E103.MirrorCS", {"start": v(33.5, 0) * mm, "end": v(33.5, 5) * mm});
            skLineSegment(sketch, "E104.MirrorCS", {"start": v(36.9, 5) * mm, "end": v(33.5, 5) * mm, "construction": true});
            skLineSegment(sketch, "E105.MirrorCS", {"start": v(33.5, 5) * mm, "end": v(35.2, 5) * mm, "construction": true});
            skLineSegment(sketch, "E106.MirrorCS", {"start": v(36.9, 10) * mm, "end": v(37.1, 10) * mm});
            skLineSegment(sketch, "E107.MirrorCS", {"start": v(36.9, 15) * mm, "end": v(37.1, 15) * mm});
            skLineSegment(sketch, "E108.MirrorCS", {"start": v(37.1, 0) * mm, "end": v(37.1, 5) * mm});
            skLineSegment(sketch, "E109.MirrorCS", {"start": v(35.2, 7.5) * mm, "end": v(33.5, 7.5) * mm, "construction": true});
            skLineSegment(sketch, "E110.MirrorCS", {"start": v(36.9, 0) * mm, "end": v(36.9, 5) * mm});
            skLineSegment(sketch, "E111.MirrorCS", {"start": v(33.3, 0) * mm, "end": v(33.3, 5) * mm});
            skLineSegment(sketch, "E112.MirrorCS", {"start": v(33.5, 15) * mm, "end": v(33.5, 10) * mm});
            skLineSegment(sketch, "E113.MirrorCS", {"start": v(35.2, 5) * mm, "end": v(35.2, 10) * mm, "construction": true});
            skLineSegment(sketch, "E114.MirrorCS", {"start": v(37.1, 15) * mm, "end": v(37.1, 10) * mm});
            skLineSegment(sketch, "E115.MirrorCS", {"start": v(35.2, 10) * mm, "end": v(35.2, 7.5) * mm, "construction": true});
            skLineSegment(sketch, "E116.MirrorCS", {"start": v(33.3, 15) * mm, "end": v(33.3, 10) * mm});
            skLineSegment(sketch, "E117.MirrorCS", {"start": v(36.9, 15) * mm, "end": v(36.9, 10) * mm});
            skSolve(sketch);
        }
        {
            var Q0;
            Q0 = qSketchRegion(id + "F8", true);
            var Q1;
            Q1=makeQuery(id+"F5.boolean.opBoolean","MERGE",FACE,{"derivedFrom":[makeQuery(id+"F3.boolean.opBoolean","MERGE",FACE,{"derivedFrom":[makeQuery(id+"F1.opExtrude","CAP_FACE",FACE,{"disambiguationData":[OSD([sQuery(id+"F0.wireOp",EDGE,"E0.bottom"),sQuery(id+"F0.wireOp",EDGE,"E0.top"),sQuery(id+"F0.wireOp",EDGE,"E0.left"),sQuery(id+"F0.wireOp",EDGE,"E0.right")])],"isStart":true}),makeQuery(id+"F3.opExtrude","CAP_FACE",FACE,{"disambiguationData":[OSD([sQuery(id+"F2.wireOp",EDGE,"E1.bottom"),sQuery(id+"F2.wireOp",EDGE,"E1.top"),sQuery(id+"F2.wireOp",EDGE,"E1.left"),sQuery(id+"F2.wireOp",EDGE,"E1.right")])],"isStart":false}),makeQuery(id+"F3.opExtrude","CAP_FACE",FACE,{"disambiguationData":[OSD([sQuery(id+"F2.wireOp",EDGE,"E2.0.1.0"),sQuery(id+"F2.wireOp",EDGE,"E2.0.1.1"),sQuery(id+"F2.wireOp",EDGE,"E2.0.1.2"),sQuery(id+"F2.wireOp",EDGE,"E2.0.1.3")])],"isStart":false}),makeQuery(id+"F3.opExtrude","CAP_FACE",FACE,{"disambiguationData":[OSD([sQuery(id+"F2.wireOp",EDGE,"E2.0.2.0"),sQuery(id+"F2.wireOp",EDGE,"E2.0.2.1"),sQuery(id+"F2.wireOp",EDGE,"E2.0.2.2"),sQuery(id+"F2.wireOp",EDGE,"E2.0.2.3")])],"isStart":false}),makeQuery(id+"F3.opExtrude","CAP_FACE",FACE,{"disambiguationData":[OSD([sQuery(id+"F2.wireOp",EDGE,"E2.0.3.0"),sQuery(id+"F2.wireOp",EDGE,"E2.0.3.1"),sQuery(id+"F2.wireOp",EDGE,"E2.0.3.2"),sQuery(id+"F2.wireOp",EDGE,"E2.0.3.3")])],"isStart":false}),makeQuery(id+"F3.opExtrude","CAP_FACE",FACE,{"disambiguationData":[OSD([sQuery(id+"F2.wireOp",EDGE,"E3.MirrorCS"),sQuery(id+"F2.wireOp",EDGE,"E4.MirrorCS"),sQuery(id+"F2.wireOp",EDGE,"E17.MirrorCS"),sQuery(id+"F2.wireOp",EDGE,"E18.MirrorCS")])],"isStart":false}),makeQuery(id+"F3.opExtrude","CAP_FACE",FACE,{"disambiguationData":[OSD([sQuery(id+"F2.wireOp",EDGE,"E5.MirrorCS"),sQuery(id+"F2.wireOp",EDGE,"E7.MirrorCS"),sQuery(id+"F2.wireOp",EDGE,"E8.MirrorCS"),sQuery(id+"F2.wireOp",EDGE,"E9.MirrorCS")])],"isStart":false}),makeQuery(id+"F3.opExtrude","CAP_FACE",FACE,{"disambiguationData":[OSD([sQuery(id+"F2.wireOp",EDGE,"E6.MirrorCS"),sQuery(id+"F2.wireOp",EDGE,"E10.MirrorCS"),sQuery(id+"F2.wireOp",EDGE,"E11.MirrorCS"),sQuery(id+"F2.wireOp",EDGE,"E13.MirrorCS")])],"isStart":false}),makeQuery(id+"F3.opExtrude","CAP_FACE",FACE,{"disambiguationData":[OSD([sQuery(id+"F2.wireOp",EDGE,"E14.MirrorCS"),sQuery(id+"F2.wireOp",EDGE,"E15.MirrorCS"),sQuery(id+"F2.wireOp",EDGE,"E16.MirrorCS"),sQuery(id+"F2.wireOp",EDGE,"E19.MirrorCS")])],"isStart":false})]}),makeQuery(id+"F5.opExtrude","CAP_FACE",FACE,{"disambiguationData":[OSD([sQuery(id+"F4.wireOp",EDGE,"E22.bottom"),sQuery(id+"F4.wireOp",EDGE,"E22.top"),sQuery(id+"F4.wireOp",EDGE,"E22.left"),sQuery(id+"F4.wireOp",EDGE,"E22.right")])],"isStart":false}),makeQuery(id+"F5.opExtrude","CAP_FACE",FACE,{"disambiguationData":[OSD([sQuery(id+"F4.wireOp",EDGE,"E23.1.0.0"),sQuery(id+"F4.wireOp",EDGE,"E23.1.0.1"),sQuery(id+"F4.wireOp",EDGE,"E23.1.0.2"),sQuery(id+"F4.wireOp",EDGE,"E23.1.0.3")])],"isStart":false}),makeQuery(id+"F5.opExtrude","CAP_FACE",FACE,{"disambiguationData":[OSD([sQuery(id+"F4.wireOp",EDGE,"E23.2.0.0"),sQuery(id+"F4.wireOp",EDGE,"E23.2.0.1"),sQuery(id+"F4.wireOp",EDGE,"E23.2.0.2"),sQuery(id+"F4.wireOp",EDGE,"E23.2.0.3")])],"isStart":false}),makeQuery(id+"F5.opExtrude","CAP_FACE",FACE,{"disambiguationData":[OSD([sQuery(id+"F4.wireOp",EDGE,"E23.3.0.0"),sQuery(id+"F4.wireOp",EDGE,"E23.3.0.1"),sQuery(id+"F4.wireOp",EDGE,"E23.3.0.2"),sQuery(id+"F4.wireOp",EDGE,"E23.3.0.3")])],"isStart":false}),makeQuery(id+"F5.opExtrude","CAP_FACE",FACE,{"disambiguationData":[OSD([sQuery(id+"F4.wireOp",EDGE,"E23.4.0.0"),sQuery(id+"F4.wireOp",EDGE,"E23.4.0.1"),sQuery(id+"F4.wireOp",EDGE,"E23.4.0.2"),sQuery(id+"F4.wireOp",EDGE,"E23.4.0.3")])],"isStart":false}),makeQuery(id+"F5.opExtrude","CAP_FACE",FACE,{"disambiguationData":[OSD([sQuery(id+"F4.wireOp",EDGE,"E24.MirrorCS"),sQuery(id+"F4.wireOp",EDGE,"E25.MirrorCS"),sQuery(id+"F4.wireOp",EDGE,"E37.MirrorCS"),sQuery(id+"F4.wireOp",EDGE,"E42.MirrorCS")])],"isStart":false}),makeQuery(id+"F5.opExtrude","CAP_FACE",FACE,{"disambiguationData":[OSD([sQuery(id+"F4.wireOp",EDGE,"E26.MirrorCS"),sQuery(id+"F4.wireOp",EDGE,"E27.MirrorCS"),sQuery(id+"F4.wireOp",EDGE,"E38.MirrorCS"),sQuery(id+"F4.wireOp",EDGE,"E39.MirrorCS")])],"isStart":false}),makeQuery(id+"F5.opExtrude","CAP_FACE",FACE,{"disambiguationData":[OSD([sQuery(id+"F4.wireOp",EDGE,"E28.MirrorCS"),sQuery(id+"F4.wireOp",EDGE,"E29.MirrorCS"),sQuery(id+"F4.wireOp",EDGE,"E34.MirrorCS"),sQuery(id+"F4.wireOp",EDGE,"E40.MirrorCS")])],"isStart":false}),makeQuery(id+"F5.opExtrude","CAP_FACE",FACE,{"disambiguationData":[OSD([sQuery(id+"F4.wireOp",EDGE,"E30.MirrorCS"),sQuery(id+"F4.wireOp",EDGE,"E32.MirrorCS"),sQuery(id+"F4.wireOp",EDGE,"E35.MirrorCS"),sQuery(id+"F4.wireOp",EDGE,"E41.MirrorCS")])],"isStart":false}),makeQuery(id+"F5.opExtrude","CAP_FACE",FACE,{"disambiguationData":[OSD([sQuery(id+"F4.wireOp",EDGE,"E31.MirrorCS"),sQuery(id+"F4.wireOp",EDGE,"E33.MirrorCS"),sQuery(id+"F4.wireOp",EDGE,"E36.MirrorCS"),sQuery(id+"F4.wireOp",EDGE,"E43.MirrorCS")])],"isStart":false})]});
            extrude(context, id + "F9", {"entities" : qUnion([Q0]), "operationType" : NewBodyOperationType.ADD, "endBound" : BoundingType.UP_TO_SURFACE, "oppositeDirection" : true, "depth" : 25 * mm, "endBoundEntityFace" : qUnion([Q1]), "offsetDistance" : 25 * mm});
        }
        {
            var Q0;
            Q0=makeQuery(id+"F9.boolean.opBoolean","MERGE",FACE,{"derivedFrom":[makeQuery(id+"F5.boolean.opBoolean","MERGE",FACE,{"derivedFrom":[makeQuery(id+"F3.boolean.opBoolean","MERGE",FACE,{"derivedFrom":[makeQuery(id+"F1.opExtrude","CAP_FACE",FACE,{"disambiguationData":[OSD([sQuery(id+"F0.wireOp",EDGE,"E0.bottom"),sQuery(id+"F0.wireOp",EDGE,"E0.top"),sQuery(id+"F0.wireOp",EDGE,"E0.left"),sQuery(id+"F0.wireOp",EDGE,"E0.right")])],"isStart":false}),makeQuery(id+"F3.opExtrude","CAP_FACE",FACE,{"disambiguationData":[OSD([sQuery(id+"F2.wireOp",EDGE,"E1.bottom"),sQuery(id+"F2.wireOp",EDGE,"E1.top"),sQuery(id+"F2.wireOp",EDGE,"E1.left"),sQuery(id+"F2.wireOp",EDGE,"E1.right")])],"isStart":true}),makeQuery(id+"F3.opExtrude","CAP_FACE",FACE,{"disambiguationData":[OSD([sQuery(id+"F2.wireOp",EDGE,"E2.0.1.0"),sQuery(id+"F2.wireOp",EDGE,"E2.0.1.1"),sQuery(id+"F2.wireOp",EDGE,"E2.0.1.2"),sQuery(id+"F2.wireOp",EDGE,"E2.0.1.3")])],"isStart":true}),makeQuery(id+"F3.opExtrude","CAP_FACE",FACE,{"disambiguationData":[OSD([sQuery(id+"F2.wireOp",EDGE,"E2.0.2.0"),sQuery(id+"F2.wireOp",EDGE,"E2.0.2.1"),sQuery(id+"F2.wireOp",EDGE,"E2.0.2.2"),sQuery(id+"F2.wireOp",EDGE,"E2.0.2.3")])],"isStart":true}),makeQuery(id+"F3.opExtrude","CAP_FACE",FACE,{"disambiguationData":[OSD([sQuery(id+"F2.wireOp",EDGE,"E2.0.3.0"),sQuery(id+"F2.wireOp",EDGE,"E2.0.3.1"),sQuery(id+"F2.wireOp",EDGE,"E2.0.3.2"),sQuery(id+"F2.wireOp",EDGE,"E2.0.3.3")])],"isStart":true}),makeQuery(id+"F3.opExtrude","CAP_FACE",FACE,{"disambiguationData":[OSD([sQuery(id+"F2.wireOp",EDGE,"E3.MirrorCS"),sQuery(id+"F2.wireOp",EDGE,"E4.MirrorCS"),sQuery(id+"F2.wireOp",EDGE,"E17.MirrorCS"),sQuery(id+"F2.wireOp",EDGE,"E18.MirrorCS")])],"isStart":true}),makeQuery(id+"F3.opExtrude","CAP_FACE",FACE,{"disambiguationData":[OSD([sQuery(id+"F2.wireOp",EDGE,"E5.MirrorCS"),sQuery(id+"F2.wireOp",EDGE,"E7.MirrorCS"),sQuery(id+"F2.wireOp",EDGE,"E8.MirrorCS"),sQuery(id+"F2.wireOp",EDGE,"E9.MirrorCS")])],"isStart":true}),makeQuery(id+"F3.opExtrude","CAP_FACE",FACE,{"disambiguationData":[OSD([sQuery(id+"F2.wireOp",EDGE,"E6.MirrorCS"),sQuery(id+"F2.wireOp",EDGE,"E10.MirrorCS"),sQuery(id+"F2.wireOp",EDGE,"E11.MirrorCS"),sQuery(id+"F2.wireOp",EDGE,"E13.MirrorCS")])],"isStart":true}),makeQuery(id+"F3.opExtrude","CAP_FACE",FACE,{"disambiguationData":[OSD([sQuery(id+"F2.wireOp",EDGE,"E14.MirrorCS"),sQuery(id+"F2.wireOp",EDGE,"E15.MirrorCS"),sQuery(id+"F2.wireOp",EDGE,"E16.MirrorCS"),sQuery(id+"F2.wireOp",EDGE,"E19.MirrorCS")])],"isStart":true})]}),makeQuery(id+"F5.opExtrude","CAP_FACE",FACE,{"disambiguationData":[OSD([sQuery(id+"F4.wireOp",EDGE,"E22.bottom"),sQuery(id+"F4.wireOp",EDGE,"E22.top"),sQuery(id+"F4.wireOp",EDGE,"E22.left"),sQuery(id+"F4.wireOp",EDGE,"E22.right")])],"isStart":true}),makeQuery(id+"F5.opExtrude","CAP_FACE",FACE,{"disambiguationData":[OSD([sQuery(id+"F4.wireOp",EDGE,"E23.1.0.0"),sQuery(id+"F4.wireOp",EDGE,"E23.1.0.1"),sQuery(id+"F4.wireOp",EDGE,"E23.1.0.2"),sQuery(id+"F4.wireOp",EDGE,"E23.1.0.3")])],"isStart":true}),makeQuery(id+"F5.opExtrude","CAP_FACE",FACE,{"disambiguationData":[OSD([sQuery(id+"F4.wireOp",EDGE,"E23.2.0.0"),sQuery(id+"F4.wireOp",EDGE,"E23.2.0.1"),sQuery(id+"F4.wireOp",EDGE,"E23.2.0.2"),sQuery(id+"F4.wireOp",EDGE,"E23.2.0.3")])],"isStart":true}),makeQuery(id+"F5.opExtrude","CAP_FACE",FACE,{"disambiguationData":[OSD([sQuery(id+"F4.wireOp",EDGE,"E23.3.0.0"),sQuery(id+"F4.wireOp",EDGE,"E23.3.0.1"),sQuery(id+"F4.wireOp",EDGE,"E23.3.0.2"),sQuery(id+"F4.wireOp",EDGE,"E23.3.0.3")])],"isStart":true}),makeQuery(id+"F5.opExtrude","CAP_FACE",FACE,{"disambiguationData":[OSD([sQuery(id+"F4.wireOp",EDGE,"E23.4.0.0"),sQuery(id+"F4.wireOp",EDGE,"E23.4.0.1"),sQuery(id+"F4.wireOp",EDGE,"E23.4.0.2"),sQuery(id+"F4.wireOp",EDGE,"E23.4.0.3")])],"isStart":true}),makeQuery(id+"F5.opExtrude","CAP_FACE",FACE,{"disambiguationData":[OSD([sQuery(id+"F4.wireOp",EDGE,"E24.MirrorCS"),sQuery(id+"F4.wireOp",EDGE,"E25.MirrorCS"),sQuery(id+"F4.wireOp",EDGE,"E37.MirrorCS"),sQuery(id+"F4.wireOp",EDGE,"E42.MirrorCS")])],"isStart":true}),makeQuery(id+"F5.opExtrude","CAP_FACE",FACE,{"disambiguationData":[OSD([sQuery(id+"F4.wireOp",EDGE,"E26.MirrorCS"),sQuery(id+"F4.wireOp",EDGE,"E27.MirrorCS"),sQuery(id+"F4.wireOp",EDGE,"E38.MirrorCS"),sQuery(id+"F4.wireOp",EDGE,"E39.MirrorCS")])],"isStart":true}),makeQuery(id+"F5.opExtrude","CAP_FACE",FACE,{"disambiguationData":[OSD([sQuery(id+"F4.wireOp",EDGE,"E28.MirrorCS"),sQuery(id+"F4.wireOp",EDGE,"E29.MirrorCS"),sQuery(id+"F4.wireOp",EDGE,"E34.MirrorCS"),sQuery(id+"F4.wireOp",EDGE,"E40.MirrorCS")])],"isStart":true}),makeQuery(id+"F5.opExtrude","CAP_FACE",FACE,{"disambiguationData":[OSD([sQuery(id+"F4.wireOp",EDGE,"E30.MirrorCS"),sQuery(id+"F4.wireOp",EDGE,"E32.MirrorCS"),sQuery(id+"F4.wireOp",EDGE,"E35.MirrorCS"),sQuery(id+"F4.wireOp",EDGE,"E41.MirrorCS")])],"isStart":true}),makeQuery(id+"F5.opExtrude","CAP_FACE",FACE,{"disambiguationData":[OSD([sQuery(id+"F4.wireOp",EDGE,"E31.MirrorCS"),sQuery(id+"F4.wireOp",EDGE,"E33.MirrorCS"),sQuery(id+"F4.wireOp",EDGE,"E36.MirrorCS"),sQuery(id+"F4.wireOp",EDGE,"E43.MirrorCS")])],"isStart":true})]}),makeQuery(id+"F9.opExtrude","CAP_FACE",FACE,{"disambiguationData":[OSD([sQuery(id+"F8.wireOp",EDGE,"E82.bottom"),sQuery(id+"F8.wireOp",EDGE,"E82.top"),sQuery(id+"F8.wireOp",EDGE,"E82.left"),sQuery(id+"F8.wireOp",EDGE,"E82.right")])],"isStart":true}),makeQuery(id+"F9.opExtrude","CAP_FACE",FACE,{"disambiguationData":[OSD([sQuery(id+"F8.wireOp",EDGE,"E83.bottom"),sQuery(id+"F8.wireOp",EDGE,"E83.top"),sQuery(id+"F8.wireOp",EDGE,"E83.left"),sQuery(id+"F8.wireOp",EDGE,"E83.right")])],"isStart":true}),makeQuery(id+"F9.opExtrude","CAP_FACE",FACE,{"disambiguationData":[OSD([sQuery(id+"F8.wireOp",EDGE,"E91.MirrorCS"),sQuery(id+"F8.wireOp",EDGE,"E92.MirrorCS"),sQuery(id+"F8.wireOp",EDGE,"E96.MirrorCS"),sQuery(id+"F8.wireOp",EDGE,"E94.MirrorCS")])],"isStart":true}),makeQuery(id+"F9.opExtrude","CAP_FACE",FACE,{"disambiguationData":[OSD([sQuery(id+"F8.wireOp",EDGE,"E90.MirrorCS"),sQuery(id+"F8.wireOp",EDGE,"E89.MirrorCS"),sQuery(id+"F8.wireOp",EDGE,"E95.MirrorCS"),sQuery(id+"F8.wireOp",EDGE,"E93.MirrorCS")])],"isStart":true}),makeQuery(id+"F9.opExtrude","CAP_FACE",FACE,{"disambiguationData":[OSD([sQuery(id+"F8.wireOp",EDGE,"E97.MirrorCS"),sQuery(id+"F8.wireOp",EDGE,"E98.MirrorCS"),sQuery(id+"F8.wireOp",EDGE,"E103.MirrorCS"),sQuery(id+"F8.wireOp",EDGE,"E111.MirrorCS")])],"isStart":true}),makeQuery(id+"F9.opExtrude","CAP_FACE",FACE,{"disambiguationData":[OSD([sQuery(id+"F8.wireOp",EDGE,"E99.MirrorCS"),sQuery(id+"F8.wireOp",EDGE,"E100.MirrorCS"),sQuery(id+"F8.wireOp",EDGE,"E108.MirrorCS"),sQuery(id+"F8.wireOp",EDGE,"E110.MirrorCS")])],"isStart":true}),makeQuery(id+"F9.opExtrude","CAP_FACE",FACE,{"disambiguationData":[OSD([sQuery(id+"F8.wireOp",EDGE,"E101.MirrorCS"),sQuery(id+"F8.wireOp",EDGE,"E102.MirrorCS"),sQuery(id+"F8.wireOp",EDGE,"E112.MirrorCS"),sQuery(id+"F8.wireOp",EDGE,"E116.MirrorCS")])],"isStart":true}),makeQuery(id+"F9.opExtrude","CAP_FACE",FACE,{"disambiguationData":[OSD([sQuery(id+"F8.wireOp",EDGE,"E106.MirrorCS"),sQuery(id+"F8.wireOp",EDGE,"E107.MirrorCS"),sQuery(id+"F8.wireOp",EDGE,"E114.MirrorCS"),sQuery(id+"F8.wireOp",EDGE,"E117.MirrorCS")])],"isStart":true})]});
            var sketch = newSketch(context, id + "F10", { "sketchPlane" : qUnion([Q0])});
            skLineSegment(sketch, "E118.bottom", {"start": v(-39.9, 15) * mm, "end": v(-40.1, 15) * mm});
            skLineSegment(sketch, "E118.top", {"start": v(-39.9, 10) * mm, "end": v(-40.1, 10) * mm});
            skLineSegment(sketch, "E118.left", {"start": v(-39.9, 15) * mm, "end": v(-39.9, 10) * mm});
            skLineSegment(sketch, "E118.right", {"start": v(-40.1, 15) * mm, "end": v(-40.1, 10) * mm});
            skLineSegment(sketch, "E119.bottom", {"start": v(-30.5, 15) * mm, "end": v(-30.3, 15) * mm});
            skLineSegment(sketch, "E119.top", {"start": v(-30.5, 10) * mm, "end": v(-30.3, 10) * mm});
            skLineSegment(sketch, "E119.left", {"start": v(-30.5, 15) * mm, "end": v(-30.5, 10) * mm});
            skLineSegment(sketch, "E119.right", {"start": v(-30.3, 15) * mm, "end": v(-30.3, 10) * mm});
            skLineSegment(sketch, "E120.bottom", {"start": v(-39.9, 5) * mm, "end": v(-40.1, 5) * mm});
            skLineSegment(sketch, "E120.top", {"start": v(-39.9, 0) * mm, "end": v(-40.1, 0) * mm});
            skLineSegment(sketch, "E120.left", {"start": v(-39.9, 5) * mm, "end": v(-39.9, 0) * mm});
            skLineSegment(sketch, "E120.right", {"start": v(-40.1, 5) * mm, "end": v(-40.1, 0) * mm});
            skLineSegment(sketch, "E121.bottom", {"start": v(-30.5, 5) * mm, "end": v(-30.3, 5) * mm});
            skLineSegment(sketch, "E121.top", {"start": v(-30.5, 0) * mm, "end": v(-30.3, 0) * mm});
            skLineSegment(sketch, "E121.left", {"start": v(-30.5, 5) * mm, "end": v(-30.5, 0) * mm});
            skLineSegment(sketch, "E121.right", {"start": v(-30.3, 5) * mm, "end": v(-30.3, 0) * mm});
            skLineSegment(sketch, "E122.bottom", {"start": v(30.5, 15) * mm, "end": v(30.3, 15) * mm});
            skLineSegment(sketch, "E122.top", {"start": v(30.5, 10) * mm, "end": v(30.3, 10) * mm});
            skLineSegment(sketch, "E122.left", {"start": v(30.5, 15) * mm, "end": v(30.5, 10) * mm});
            skLineSegment(sketch, "E122.right", {"start": v(30.3, 15) * mm, "end": v(30.3, 10) * mm});
            skLineSegment(sketch, "E123.bottom", {"start": v(30.5, 5) * mm, "end": v(30.3, 5) * mm});
            skLineSegment(sketch, "E123.top", {"start": v(30.5, 0) * mm, "end": v(30.3, 0) * mm});
            skLineSegment(sketch, "E123.left", {"start": v(30.5, 5) * mm, "end": v(30.5, 0) * mm});
            skLineSegment(sketch, "E123.right", {"start": v(30.3, 5) * mm, "end": v(30.3, 0) * mm});
            skLineSegment(sketch, "E124.bottom", {"start": v(39.9, 15) * mm, "end": v(40.1, 15) * mm});
            skLineSegment(sketch, "E124.top", {"start": v(39.9, 10) * mm, "end": v(40.1, 10) * mm});
            skLineSegment(sketch, "E124.left", {"start": v(39.9, 15) * mm, "end": v(39.9, 10) * mm});
            skLineSegment(sketch, "E124.right", {"start": v(40.1, 15) * mm, "end": v(40.1, 10) * mm});
            skLineSegment(sketch, "E125.bottom", {"start": v(39.9, 5) * mm, "end": v(40.1, 5) * mm});
            skLineSegment(sketch, "E125.top", {"start": v(39.9, 0) * mm, "end": v(40.1, 0) * mm});
            skLineSegment(sketch, "E125.left", {"start": v(39.9, 5) * mm, "end": v(39.9, 0) * mm});
            skLineSegment(sketch, "E125.right", {"start": v(40.1, 5) * mm, "end": v(40.1, 0) * mm});
            skSolve(sketch);
        }
        {
            var Q0;
            Q0 = qSketchRegion(id + "F10", true);
            extrude(context, id + "F11", {"entities" : qUnion([Q0]), "operationType" : NewBodyOperationType.REMOVE, "endBound" : BoundingType.THROUGH_ALL, "oppositeDirection" : true, "depth" : 25 * mm, "offsetDistance" : 25 * mm});
        }
    });
